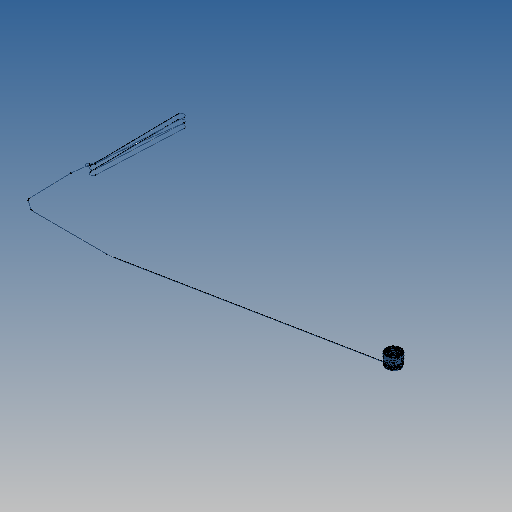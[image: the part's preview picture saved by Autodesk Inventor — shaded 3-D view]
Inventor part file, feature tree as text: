
AUTODESK INVENTOR PART (.ipt)
format: ipt  version: 2025.1 (Build 291241000, 241)  size: 603,136 bytes
history: native  units: mm
features: other x24, sketch x16, plane x13, sweep x5, loft x5, extrude x1
ambient origin geometry x8: Origin, YZ Plane, XZ Plane, XY Plane, X Axis, Y Axis, Z Axis, Center Point
bodies: Volumenkörper1 (feature_tree)
feature tree (64):
  sketch  "Skizze1"  dims[d0=25.0mm d1=384.13mm]
  plane  "Arbeitsebene2"
  plane  "Arbeitsebene3"
  sketch  "Skizze2"  dims[d2=84.152mm d3=7.2mm]
  plane  "Arbeitsebene4"
  sweep  "Sweeping1"
  sketch  "Skizze4"  dims[d6=8.0mm d7=494.83mm]
  plane  "Arbeitsebene5"
  sweep  "Sweeping2"
  sketch  "Skizze6"  dims[d10=147.858mm d11=8.406mm]
  sweep  "Sweeping3"
  plane  "Arbeitsebene6"
  loft  "Erhebung1"
  loft  "Erhebung2"
  other  "Arbeitsachse1"
  other  "Arbeitsachse2"
  plane  "Arbeitsebene7"
  sweep  "Sweeping4"
  sketch  "Skizze11"  dims[d21=0.5mm d22=0.5mm]
  other  "Arbeitspunkt2"
  other  "Arbeitspunkt3"
  other  "Arbeitsachse4"
  plane  "Arbeitsebene9"
  sweep  "Sweeping5"
  plane  "Arbeitsebene11"
  other  "Spirale1"
  sketch  "Skizze13"  dims[d24=0.01mm]
  plane  "Arbeitsebene12"
  other  "Spirale2"
  loft  "Erhebung3"
  sketch  "Skizze15"  dims[d26=1.0mm]
  plane  "Arbeitsebene13"
  other  "Spirale3"
  loft  "Erhebung4"
  loft  "Erhebung5"
  plane  "Arbeitsebene1"
  sketch  "Skizze3"  dims[d4=87.493mm d5=507.799mm]
  sketch  "Skizze5"  dims[d8=96.863mm d9=15.202mm]
  sketch  "Skizze7"  dims[d12=503.39mm d13=512.484mm]
  other  "Kanten1"
  other  "Kanten2"
  other  "Kanten3"
  other  "Kanten4"
  other  "Arbeitspunkt1"
  other  "Arbeitsachse3"
  sketch  "Skizze8"  dims[d14=496.979mm d15=8.0mm d16=8.0mm]
  sketch  "Skizze9"  dims[d17=8.0mm d18=4.8mm]
  other  "Arbeitsachse5"
  plane  "Arbeitsebene8"
  sketch  "Skizze10"  dims[d19=8.0mm d20=8.0mm]
  plane  "Arbeitsebene10"
  other  "Arbeitsachse6"
  other  "Flä1"
  sketch  "Skizze12"  dims[d23=4.0mm]
  sketch  "Skizze14"  dims[d25=0.02mm]
  other  "Kanten7"
  other  "Kanten8"
  sketch  "Skizze16"  dims[d27=0.0mm d28=0.0mm d29=0.992415mm d30=0.892415mm d31=0.5mm d32=1.0mm d33=0.0mm d34=0.0mm d35=0.5mm d36=0.5mm d37=1.0mm d38=0.0mm d39=0.0mm d40=2.5mm d41=90.0deg d42=2.5mm d43=90.0deg d44=2.5mm d45=90.0deg d46=2.5mm d47=90.0deg d48=90.0deg d49=0.5mm d50=0.5mm d52=0.0mm d53=0.0mm d54=90.0deg d55=1.0mm d56=9.0mm d57=30.0mm d58=0.0mm d59=0.0mm d60=0.0mm d61=0.5mm d62=1.0mm d63=1.001mm d64=9.3mm d65=10.0mm d66=0.0mm d67=90.0deg d68=90.0deg d69=0.0mm d70=0.0mm d71=90.0deg d72=11.5mm d73=1.0mm d74=1.001mm d75=18.7mm d76=10.0mm d77=0.0mm d78=90.0deg d79=90.0deg d80=0.0mm d81=0.0mm d82=10.0mm d83=90.0deg d84=12.5mm d85=90.0deg d86=90.0deg d87=1.0mm d88=10.5mm d89=1.001mm d90=18.5mm d91=10.0mm d92=0.0mm d93=90.0deg d94=90.0deg d95=0.0mm d96=0.0mm d97=12.5mm d98=90.0deg d99=10.0mm d100=90.0deg d101=0.0mm d102=90.0deg d103=0.0mm d104=90.0deg]
  other  "Kanten9"
  other  "Kanten10"
  other  "Kanten11"
  other  "Kanten12"
  extrude  "Extrusionsfläche1"  Depth=0.5mm
  other  "Schnittkanten projizieren1"
